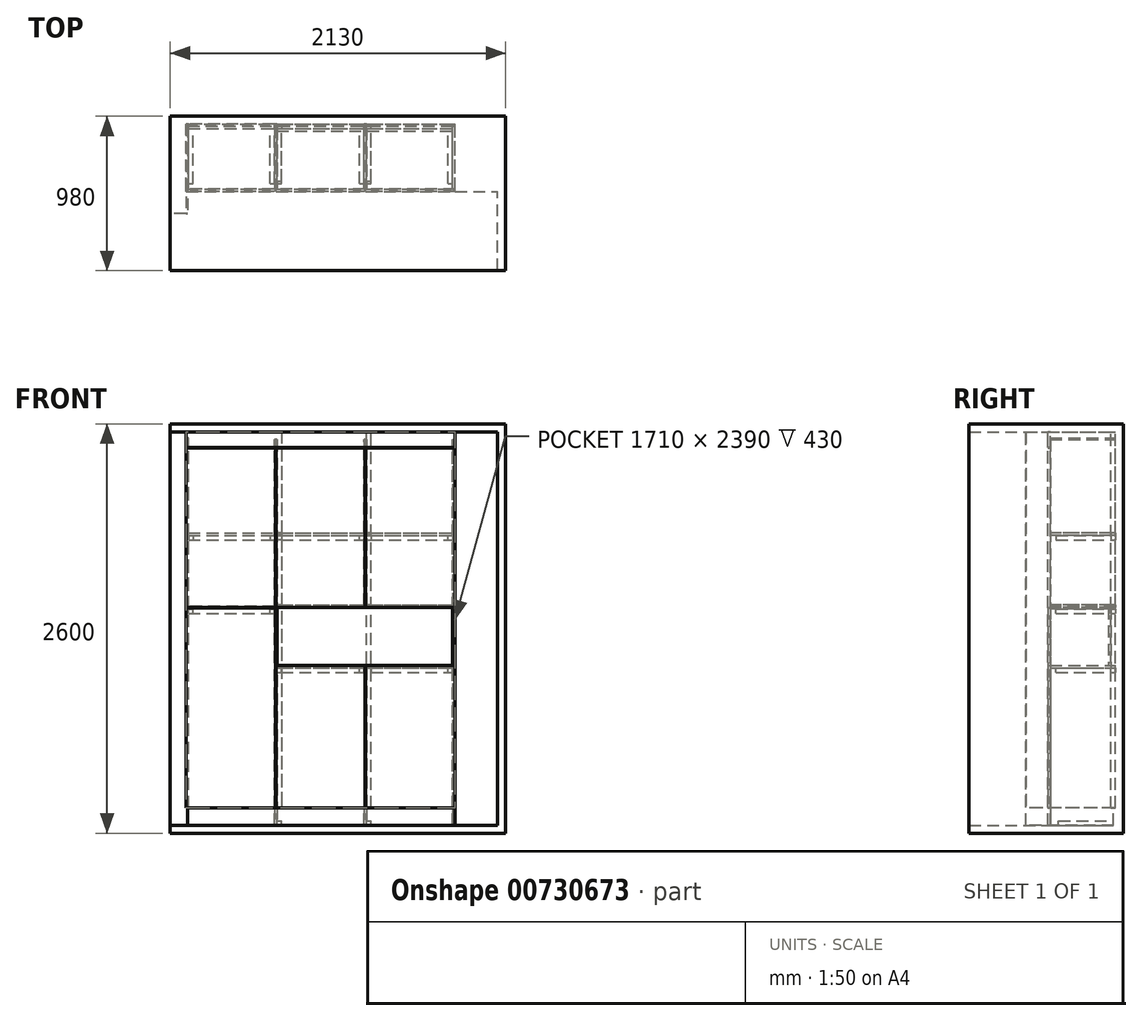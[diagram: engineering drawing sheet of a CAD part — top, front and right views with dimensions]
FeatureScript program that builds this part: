
annotation { "Feature Type Name" : "Feature", "Feature Type Description" : "" }
export const myFeature = defineFeature(function(context is Context, id is Id, definition is map)
    precondition{}
    {
        {
            var Q0;
            Q0=qCreatedBy(makeId("Front.planeOp"),FACE);
            var sketch = newSketch(context, id + "F0", { "sketchPlane" : qUnion([Q0])});
            skLineSegment(sketch, "E0.bottom", {"start": v(0, 0) * mm, "end": v(1710, 0) * mm});
            skLineSegment(sketch, "E0.top", {"start": v(0, 2500) * mm, "end": v(1710, 2500) * mm});
            skLineSegment(sketch, "E0.left", {"start": v(0, 0) * mm, "end": v(0, 2500) * mm});
            skLineSegment(sketch, "E0.right", {"start": v(1710, 0) * mm, "end": v(1710, 2500) * mm});
            skLineSegment(sketch, "E1", {"start": v(1980, -50) * mm, "end": v(-100, -50) * mm});
            skLineSegment(sketch, "E2", {"start": v(-100, -50) * mm, "end": v(-100, 2550) * mm});
            skLineSegment(sketch, "E3", {"start": v(-100, 2550) * mm, "end": v(1980, 2550) * mm});
            skLineSegment(sketch, "E4", {"start": v(1980, 2550) * mm, "end": v(1980, -50) * mm});
            skSolve(sketch);
        }
        {
            var Q0;
            Q0 = qSketchRegion(id + "F0", true);
            extrude(context, id + "F1", {"entities" : qUnion([Q0]), "depth" : 430 * mm, "offsetDistance" : 25 * mm});
        }
        {
            var Q0;
            Q0=makeQuery(id+"F1.opExtrude","CAP_FACE",FACE,{"disambiguationData":[OSD([sQuery(id+"F0.wireOp",EDGE,"E0.bottom"),sQuery(id+"F0.wireOp",EDGE,"E0.top"),sQuery(id+"F0.wireOp",EDGE,"E0.left"),sQuery(id+"F0.wireOp",EDGE,"E0.right"),sQuery(id+"F0.wireOp",EDGE,"E1"),sQuery(id+"F0.wireOp",EDGE,"E2"),sQuery(id+"F0.wireOp",EDGE,"E3"),sQuery(id+"F0.wireOp",EDGE,"E4")])],"isStart":false});
            var sketch = newSketch(context, id + "F2", { "sketchPlane" : qUnion([Q0])});
            skLineSegment(sketch, "E5.bottom", {"start": v(-100, 2550) * mm, "end": v(0, 2550) * mm});
            skLineSegment(sketch, "E5.top", {"start": v(-100, -50) * mm, "end": v(0, -50) * mm});
            skLineSegment(sketch, "E5.left", {"start": v(-100, 2550) * mm, "end": v(-100, -50) * mm});
            skLineSegment(sketch, "E5.right", {"start": v(0, 2550) * mm, "end": v(0, -50) * mm});
            skSolve(sketch);
        }
        {
            var Q0;
            Q0 = qSketchRegion(id + "F2", true);
            extrude(context, id + "F3", {"entities" : qUnion([Q0]), "operationType" : NewBodyOperationType.ADD, "depth" : (570 - 430) * mm, "offsetDistance" : 25 * mm});
        }
        {
            var Q0;
            Q0=makeQuery(id+"F1.opExtrude","CAP_FACE",FACE,{"disambiguationData":[OSD([sQuery(id+"F0.wireOp",EDGE,"E0.bottom"),sQuery(id+"F0.wireOp",EDGE,"E0.top"),sQuery(id+"F0.wireOp",EDGE,"E0.left"),sQuery(id+"F0.wireOp",EDGE,"E0.right"),sQuery(id+"F0.wireOp",EDGE,"E1"),sQuery(id+"F0.wireOp",EDGE,"E2"),sQuery(id+"F0.wireOp",EDGE,"E3"),sQuery(id+"F0.wireOp",EDGE,"E4")])],"isStart":false});
            var sketch = newSketch(context, id + "F4", { "sketchPlane" : qUnion([Q0])});
            skLineSegment(sketch, "E6", {"start": v(1980, 2550) * mm, "end": v(1980, 2500) * mm});
            skLineSegment(sketch, "E7", {"start": v(1980, -50) * mm, "end": v(-100, -50) * mm});
            skLineSegment(sketch, "E8", {"start": v(-100, 2550) * mm, "end": v(1980, 2550) * mm});
            skLineSegment(sketch, "E9", {"start": v(-100, 2550) * mm, "end": v(-100, 2500) * mm});
            skLineSegment(sketch, "E10", {"start": v(-100, 2500) * mm, "end": v(1980, 2500) * mm});
            skLineSegment(sketch, "E11", {"start": v(-100, -50) * mm, "end": v(-100, 0) * mm});
            skLineSegment(sketch, "E12", {"start": v(-100, 0) * mm, "end": v(1980, 0) * mm});
            skLineSegment(sketch, "E13.trimOffspring", {"start": v(1980, 0) * mm, "end": v(1980, -50) * mm});
            skSolve(sketch);
        }
        {
            var Q0;
            Q0 = qSketchRegion(id + "F4", true);
            extrude(context, id + "F5", {"entities" : qUnion([Q0]), "operationType" : NewBodyOperationType.ADD, "depth" : 500 * mm, "offsetDistance" : 25 * mm});
        }
        {
            var Q0;
            Q0=makeQuery(id+"F5.boolean.opBoolean","MERGE",FACE,{"derivedFrom":[makeQuery(id+"F1.opExtrude","SWEPT_FACE",FACE,{"disambiguationData":[OSD([sQuery(id+"F0.wireOp",EDGE,"E4")])]}),makeQuery(id+"F5.opExtrude","SWEPT_FACE",FACE,{"disambiguationData":[OSD([sQuery(id+"F4.wireOp",EDGE,"E6")])]}),makeQuery(id+"F5.opExtrude","SWEPT_FACE",FACE,{"disambiguationData":[OSD([sQuery(id+"F4.wireOp",EDGE,"E13.trimOffspring")])]})]});
            var sketch = newSketch(context, id + "F6", { "sketchPlane" : qUnion([Q0])});
            skLineSegment(sketch, "E14.bottom", {"start": v(-930, 2550) * mm, "end": v(0, 2550) * mm});
            skLineSegment(sketch, "E14.top", {"start": v(-930, -50) * mm, "end": v(0, -50) * mm});
            skLineSegment(sketch, "E14.left", {"start": v(-930, 2550) * mm, "end": v(-930, -50) * mm});
            skLineSegment(sketch, "E14.right", {"start": v(0, 2550) * mm, "end": v(0, -50) * mm});
            skSolve(sketch);
        }
        {
            var Q0;
            Q0 = qSketchRegion(id + "F6", true);
            extrude(context, id + "F7", {"entities" : qUnion([Q0]), "operationType" : NewBodyOperationType.ADD, "depth" : 50 * mm, "offsetDistance" : 25 * mm});
        }
        {
            var Q0;
            Q0=makeQuery(id+"F7.boolean.opBoolean","MERGE",FACE,{"derivedFrom":[makeQuery(id+"F1.opExtrude","CAP_FACE",FACE,{"disambiguationData":[OSD([sQuery(id+"F0.wireOp",EDGE,"E0.bottom"),sQuery(id+"F0.wireOp",EDGE,"E0.top"),sQuery(id+"F0.wireOp",EDGE,"E0.left"),sQuery(id+"F0.wireOp",EDGE,"E0.right"),sQuery(id+"F0.wireOp",EDGE,"E1"),sQuery(id+"F0.wireOp",EDGE,"E2"),sQuery(id+"F0.wireOp",EDGE,"E3"),sQuery(id+"F0.wireOp",EDGE,"E4")])],"isStart":true}),makeQuery(id+"F7.opExtrude","SWEPT_FACE",FACE,{"disambiguationData":[OSD([sQuery(id+"F6.wireOp",EDGE,"E14.right")])]})]});
            var sketch = newSketch(context, id + "F8", { "sketchPlane" : qUnion([Q0])});
            skLineSegment(sketch, "E15.bottom", {"start": v(-2030, 2550) * mm, "end": v(100, 2550) * mm});
            skLineSegment(sketch, "E15.top", {"start": v(-2030, -50) * mm, "end": v(100, -50) * mm});
            skLineSegment(sketch, "E15.left", {"start": v(-2030, 2550) * mm, "end": v(-2030, -50) * mm});
            skLineSegment(sketch, "E15.right", {"start": v(100, 2550) * mm, "end": v(100, -50) * mm});
            skSolve(sketch);
        }
        {
            var Q0;
            Q0 = qSketchRegion(id + "F8", true);
            extrude(context, id + "F9", {"entities" : qUnion([Q0]), "operationType" : NewBodyOperationType.ADD, "depth" : 50 * mm, "offsetDistance" : 25 * mm});
        }
        {
            var Q0;
            Q0=makeQuery(id+"F5.boolean.opBoolean","MERGE",FACE,{"derivedFrom":[makeQuery(id+"F1.opExtrude","SWEPT_FACE",FACE,{"disambiguationData":[OSD([sQuery(id+"F0.wireOp",EDGE,"E0.bottom")])]}),makeQuery(id+"F5.opExtrude","SWEPT_FACE",FACE,{"disambiguationData":[OSD([sQuery(id+"F4.wireOp",EDGE,"E12")])]})]});
            var sketch = newSketch(context, id + "F10", { "sketchPlane" : qUnion([Q0])});
            skLineSegment(sketch, "E16", {"start": v(0, 0) * mm, "end": v(570, 0) * mm});
            skLineSegment(sketch, "E17", {"start": v(570, 0) * mm, "end": v(1140, 0) * mm});
            skLineSegment(sketch, "E18", {"start": v(1140, 0) * mm, "end": v(1710, 0) * mm});
            skSolve(sketch);
        }
        {
            var Q0;
            Q0=makeQuery(id+"F3.opExtrude","CAP_FACE",FACE,{"disambiguationData":[OSD([sQuery(id+"F2.wireOp",EDGE,"E5.bottom"),sQuery(id+"F2.wireOp",EDGE,"E5.top"),sQuery(id+"F2.wireOp",EDGE,"E5.left"),sQuery(id+"F2.wireOp",EDGE,"E5.right")])],"isStart":false});
            var sketch = newSketch(context, id + "F11", { "sketchPlane" : qUnion([Q0])});
            skLineSegment(sketch, "E19.bottom", {"start": v(0, 0) * mm, "end": v(10, 0) * mm});
            skLineSegment(sketch, "E19.top", {"start": v(0, 110) * mm, "end": v(10, 110) * mm});
            skLineSegment(sketch, "E19.left", {"start": v(0, 0) * mm, "end": v(0, 110) * mm});
            skLineSegment(sketch, "E19.right", {"start": v(10, 0) * mm, "end": v(10, 110) * mm});
            skSolve(sketch);
        }
        {
            var Q0;
            Q0 = qSketchRegion(id + "F11", true);
            var Q1;
            Q1=makeQuery(id+"F9.opExtrude","CAP_FACE",FACE,{"disambiguationData":[OSD([sQuery(id+"F8.wireOp",EDGE,"E15.bottom"),sQuery(id+"F8.wireOp",EDGE,"E15.top"),sQuery(id+"F8.wireOp",EDGE,"E15.left"),sQuery(id+"F8.wireOp",EDGE,"E15.right")])],"isStart":true});
            extrude(context, id + "F12", {"entities" : qUnion([Q0]), "endBound" : BoundingType.UP_TO_SURFACE, "oppositeDirection" : true, "depth" : 25 * mm, "endBoundEntityFace" : qUnion([Q1]), "offsetDistance" : 25 * mm});
        }
        {
            var Q0;
            Q0=makeQuery(id+"F9.opExtrude","CAP_FACE",FACE,{"disambiguationData":[OSD([sQuery(id+"F8.wireOp",EDGE,"E15.bottom"),sQuery(id+"F8.wireOp",EDGE,"E15.top"),sQuery(id+"F8.wireOp",EDGE,"E15.left"),sQuery(id+"F8.wireOp",EDGE,"E15.right")])],"isStart":true});
            var sketch = newSketch(context, id + "F13", { "sketchPlane" : qUnion([Q0])});
            skLineSegment(sketch, "E20.bottom", {"start": v(10, 110) * mm, "end": v(1710, 110) * mm});
            skLineSegment(sketch, "E20.top", {"start": v(10, 0) * mm, "end": v(1710, 0) * mm});
            skLineSegment(sketch, "E20.left", {"start": v(10, 110) * mm, "end": v(10, 0) * mm});
            skLineSegment(sketch, "E20.right", {"start": v(1710, 110) * mm, "end": v(1710, 0) * mm});
            skSolve(sketch);
        }
        {
            var Q0;
            Q0 = qSketchRegion(id + "F13", true);
            extrude(context, id + "F14", {"entities" : qUnion([Q0]), "operationType" : NewBodyOperationType.ADD, "depth" : 12 * mm, "offsetDistance" : 25 * mm});
        }
        {
            var Q0;
            Q0=makeQuery(id+"F1.opExtrude","CAP_FACE",FACE,{"disambiguationData":[OSD([sQuery(id+"F0.wireOp",EDGE,"E0.bottom"),sQuery(id+"F0.wireOp",EDGE,"E0.top"),sQuery(id+"F0.wireOp",EDGE,"E0.left"),sQuery(id+"F0.wireOp",EDGE,"E0.right"),sQuery(id+"F0.wireOp",EDGE,"E1"),sQuery(id+"F0.wireOp",EDGE,"E2"),sQuery(id+"F0.wireOp",EDGE,"E3"),sQuery(id+"F0.wireOp",EDGE,"E4")])],"isStart":false});
            var sketch = newSketch(context, id + "F15", { "sketchPlane" : qUnion([Q0])});
            skLineSegment(sketch, "E21.bottom", {"start": v(1710, 2500) * mm, "end": v(0, 2500) * mm});
            skLineSegment(sketch, "E21.top", {"start": v(1710, 2400) * mm, "end": v(0, 2400) * mm});
            skLineSegment(sketch, "E21.left", {"start": v(1710, 2500) * mm, "end": v(1710, 2400) * mm});
            skLineSegment(sketch, "E21.right", {"start": v(0, 2500) * mm, "end": v(0, 2400) * mm});
            skSolve(sketch);
        }
        {
            var Q0;
            Q0 = qSketchRegion(id + "F15", true);
            extrude(context, id + "F16", {"entities" : qUnion([Q0]), "oppositeDirection" : true, "depth" : 16 * mm, "offsetDistance" : 25 * mm});
        }
        {
            var Q0;
            Q0=makeQuery(id+"F3.boolean.opBoolean","MERGE",FACE,{"derivedFrom":[makeQuery(id+"F1.opExtrude","SWEPT_FACE",FACE,{"disambiguationData":[OSD([sQuery(id+"F0.wireOp",EDGE,"E0.left")])]}),makeQuery(id+"F3.opExtrude","SWEPT_FACE",FACE,{"disambiguationData":[OSD([sQuery(id+"F2.wireOp",EDGE,"E5.right")])]})]});
            var sketch = newSketch(context, id + "F17", { "sketchPlane" : qUnion([Q0])});
            skLineSegment(sketch, "E22.bottom", {"start": v(-414, 110) * mm, "end": v(0, 110) * mm});
            skLineSegment(sketch, "E22.top", {"start": v(-414, 2460) * mm, "end": v(0, 2460) * mm});
            skLineSegment(sketch, "E22.left", {"start": v(-414, 110) * mm, "end": v(-414, 2460) * mm});
            skLineSegment(sketch, "E22.right", {"start": v(0, 110) * mm, "end": v(0, 2460) * mm});
            skSolve(sketch);
        }
        {
            var Q0;
            Q0 = qSketchRegion(id + "F17", true);
            extrude(context, id + "F18", {"entities" : qUnion([Q0]), "depth" : 16 * mm, "offsetDistance" : 25 * mm});
        }
        {
            var Q0;
            Q0=sQuery(id+"F10.wireOp",VERTEX,"E17.start");
            var Q1;
            Q1=sQuery(id+"F10.wireOp",EDGE,"E16");
            cPlane(context, id + "F19", {"entities" : qUnion([Q0, Q1]), "cplaneType" : CPlaneType.LINE_POINT, "offset" : 25 * mm, "width" : 150 * mm, "height" : 150 * mm});
        }
        {
            var Q0;
            Q0=sQuery(id+"F10.wireOp",VERTEX,"E18.start");
            var Q1;
            Q1=sQuery(id+"F10.wireOp",EDGE,"E17");
            cPlane(context, id + "F20", {"entities" : qUnion([Q0, Q1]), "cplaneType" : CPlaneType.LINE_POINT, "offset" : 25 * mm, "width" : 150 * mm, "height" : 150 * mm});
        }
        {
            var Q0;
            Q0=qCreatedBy(id+"F19.planeOp",FACE);
            var sketch = newSketch(context, id + "F21", { "sketchPlane" : qUnion([Q0])});
            skLineSegment(sketch, "E23", {"start": v(-414, 0) * mm, "end": v(-414, 2450) * mm});
            skLineSegment(sketch, "E24", {"start": v(-414, 2450) * mm, "end": v(0, 2450) * mm});
            skLineSegment(sketch, "E25", {"start": v(0, 2450) * mm, "end": v(0, 112) * mm});
            skLineSegment(sketch, "E26", {"start": v(0, 112) * mm, "end": v(-14, 112) * mm});
            skLineSegment(sketch, "E27", {"start": v(-14, 112) * mm, "end": v(-14, 0) * mm});
            skLineSegment(sketch, "E28", {"start": v(-14, 0) * mm, "end": v(-414, 0) * mm});
            skPoint(sketch, "E29", {"position": v(0, 110) * mm});
            skPoint(sketch, "E30", {"position": v(-12, 0) * mm});
            skPoint(sketch, "E31", {"position": v(0, 2500) * mm});
            skSolve(sketch);
        }
        {
            var Q0;
            Q0 = qSketchRegion(id + "F21", true);
            extrude(context, id + "F22", {"entities" : qUnion([Q0]), "endBound" : BoundingType.SYMMETRIC, "depth" : 16 * mm, "offsetDistance" : 25 * mm});
        }
        {
            var Q0;
            Q0=qCreatedBy(id+"F20.planeOp",FACE);
            var sketch = newSketch(context, id + "F23", { "sketchPlane" : qUnion([Q0])});
            skLineSegment(sketch, "E32.0.0", {"start": v(-414, 0) * mm, "end": v(-14, 0) * mm});
            skLineSegment(sketch, "E32.0.1", {"start": v(-14, 0) * mm, "end": v(-14, 112) * mm});
            skLineSegment(sketch, "E32.0.2", {"start": v(-14, 112) * mm, "end": v(0, 112) * mm});
            skLineSegment(sketch, "E32.0.3", {"start": v(0, 112) * mm, "end": v(0, 1000) * mm});
            skLineSegment(sketch, "E32.0.4", {"start": v(0, 2450) * mm, "end": v(-414, 2450) * mm});
            skLineSegment(sketch, "E32.0.5", {"start": v(-414, 2450) * mm, "end": v(-414, 1400) * mm});
            skLineSegment(sketch, "E33", {"start": v(-414, 1000) * mm, "end": v(0, 1000) * mm});
            skLineSegment(sketch, "E34", {"start": v(-414, 1400) * mm, "end": v(0, 1400) * mm});
            skLineSegment(sketch, "E35.trimOffspring", {"start": v(-414, 1000) * mm, "end": v(-414, 0) * mm});
            skLineSegment(sketch, "E36.trimOffspring", {"start": v(0, 1400) * mm, "end": v(0, 2450) * mm});
            skSolve(sketch);
        }
        {
            var Q0;
            Q0 = qSketchRegion(id + "F23", true);
            extrude(context, id + "F24", {"entities" : qUnion([Q0]), "endBound" : BoundingType.SYMMETRIC, "depth" : 16 * mm, "offsetDistance" : 25 * mm});
        }
        {
            var Q0;
            Q0=makeQuery(id+"F1.opExtrude","SWEPT_FACE",FACE,{"disambiguationData":[OSD([sQuery(id+"F0.wireOp",EDGE,"E0.right")])]});
            var sketch = newSketch(context, id + "F25", { "sketchPlane" : qUnion([Q0])});
            skLineSegment(sketch, "E37.0", {"start": v(414, 2450) * mm, "end": v(0, 2450) * mm});
            skLineSegment(sketch, "E38", {"start": v(414, 2450) * mm, "end": v(414, 0) * mm});
            skLineSegment(sketch, "E39", {"start": v(414, 0) * mm, "end": v(14, 0) * mm});
            skLineSegment(sketch, "E40", {"start": v(14, 0) * mm, "end": v(14, 112) * mm});
            skLineSegment(sketch, "E41", {"start": v(14, 112) * mm, "end": v(0, 112) * mm});
            skLineSegment(sketch, "E42", {"start": v(0, 112) * mm, "end": v(0, 2450) * mm});
            skSolve(sketch);
        }
        {
            var Q0;
            Q0 = qSketchRegion(id + "F25", true);
            extrude(context, id + "F26", {"entities" : qUnion([Q0]), "depth" : 16 * mm, "offsetDistance" : 25 * mm});
        }
        {
            var Q0;
            Q0=makeQuery(id+"F24.opExtrude","SWEPT_FACE",FACE,{"disambiguationData":[OSD([sQuery(id+"F23.wireOp",EDGE,"E34")])]});
            var sketch = newSketch(context, id + "F27", { "sketchPlane" : qUnion([Q0])});
            skLineSegment(sketch, "E43.bottom", {"start": v(578, 0) * mm, "end": v(1694, 0) * mm});
            skLineSegment(sketch, "E43.top", {"start": v(578, 414) * mm, "end": v(1694, 414) * mm});
            skLineSegment(sketch, "E43.left", {"start": v(578, 0) * mm, "end": v(578, 414) * mm});
            skLineSegment(sketch, "E43.right", {"start": v(1694, 0) * mm, "end": v(1694, 414) * mm});
            skSolve(sketch);
        }
        {
            var Q0;
            Q0 = qSketchRegion(id + "F27", true);
            extrude(context, id + "F28", {"entities" : qUnion([Q0]), "depth" : 16 * mm, "offsetDistance" : 25 * mm});
        }
        {
            var Q0;
            Q0=makeQuery(id+"F24.opExtrude","SWEPT_FACE",FACE,{"disambiguationData":[OSD([sQuery(id+"F23.wireOp",EDGE,"E33")])]});
            var sketch = newSketch(context, id + "F29", { "sketchPlane" : qUnion([Q0])});
            skLineSegment(sketch, "E44.bottom", {"start": v(578, -414) * mm, "end": v(1694, -414) * mm});
            skLineSegment(sketch, "E44.top", {"start": v(578, 0) * mm, "end": v(1694, 0) * mm});
            skLineSegment(sketch, "E44.left", {"start": v(578, -414) * mm, "end": v(578, 0) * mm});
            skLineSegment(sketch, "E44.right", {"start": v(1694, -414) * mm, "end": v(1694, 0) * mm});
            skSolve(sketch);
        }
        {
            var Q0;
            Q0 = qSketchRegion(id + "F29", true);
            extrude(context, id + "F30", {"entities" : qUnion([Q0]), "depth" : 16 * mm, "offsetDistance" : 25 * mm});
        }
        {
            var Q0;
            Q0=makeQuery(id+"F22.opExtrude","SWEPT_FACE",FACE,{"disambiguationData":[OSD([sQuery(id+"F21.wireOp",EDGE,"E23")])]});
            var sketch = newSketch(context, id + "F31", { "sketchPlane" : qUnion([Q0])});
            skLineSegment(sketch, "E45.bottom", {"start": v(1710, 0) * mm, "end": v(10, 0) * mm});
            skLineSegment(sketch, "E45.top", {"start": v(1710, 110) * mm, "end": v(10, 110) * mm});
            skLineSegment(sketch, "E45.left", {"start": v(1710, 0) * mm, "end": v(1710, 110) * mm});
            skLineSegment(sketch, "E45.right", {"start": v(10, 0) * mm, "end": v(10, 110) * mm});
            skSolve(sketch);
        }
        {
            var Q0;
            Q0 = qSketchRegion(id + "F31", true);
            extrude(context, id + "F32", {"entities" : qUnion([Q0]), "depth" : 16 * mm, "offsetDistance" : 25 * mm});
        }
        {
            var Q0;
            Q0=makeQuery(id+"F28.opExtrude","CAP_FACE",FACE,{"disambiguationData":[OSD([sQuery(id+"F27.wireOp",EDGE,"E43.bottom"),sQuery(id+"F27.wireOp",EDGE,"E43.top"),sQuery(id+"F27.wireOp",EDGE,"E43.left"),sQuery(id+"F27.wireOp",EDGE,"E43.right")])],"isStart":true});
            cPlane(context, id + "F33", {"entities" : qUnion([Q0]), "cplaneType" : CPlaneType.OFFSET, "offset" : 9 * mm, "oppositeDirection" : true, "width" : 150 * mm, "height" : 150 * mm});
        }
        {
            var Q0;
            Q0=qCreatedBy(id+"F33.planeOp",FACE);
            var sketch = newSketch(context, id + "F34", { "sketchPlane" : qUnion([Q0])});
            skLineSegment(sketch, "E46.bottom", {"start": v(562, 0) * mm, "end": v(16, 0) * mm});
            skLineSegment(sketch, "E46.top", {"start": v(562, -414) * mm, "end": v(16, -414) * mm});
            skLineSegment(sketch, "E46.left", {"start": v(562, 0) * mm, "end": v(562, -414) * mm});
            skLineSegment(sketch, "E46.right", {"start": v(16, 0) * mm, "end": v(16, -414) * mm});
            skSolve(sketch);
        }
        {
            var Q0;
            Q0 = qSketchRegion(id + "F34", true);
            extrude(context, id + "F35", {"entities" : qUnion([Q0]), "oppositeDirection" : true, "depth" : 16 * mm, "offsetDistance" : 25 * mm});
        }
        {
            var Q0;
            Q0=makeQuery(id+"F22.opExtrude","SWEPT_FACE",FACE,{"disambiguationData":[OSD([sQuery(id+"F21.wireOp",EDGE,"E23")])]});
            var sketch = newSketch(context, id + "F36", { "sketchPlane" : qUnion([Q0])});
            skLineSegment(sketch, "E47.bottom", {"start": v(2, 2398) * mm, "end": v(568, 2398) * mm});
            skLineSegment(sketch, "E47.top", {"start": v(2, 1384) * mm, "end": v(568, 1384) * mm});
            skLineSegment(sketch, "E47.left", {"start": v(2, 2398) * mm, "end": v(2, 1384) * mm});
            skLineSegment(sketch, "E47.right", {"start": v(568, 2398) * mm, "end": v(568, 1384) * mm});
            skLineSegment(sketch, "E48", {"start": v(562, 1400) * mm, "end": v(578, 1400) * mm, "construction": true});
            skPoint(sketch, "E49", {"position": v(570, 1400) * mm});
            skLineSegment(sketch, "E50.bottom", {"start": v(572, 1384) * mm, "end": v(1138, 1384) * mm});
            skLineSegment(sketch, "E50.top", {"start": v(572, 2398) * mm, "end": v(1138, 2398) * mm});
            skLineSegment(sketch, "E50.left", {"start": v(572, 1384) * mm, "end": v(572, 2398) * mm});
            skLineSegment(sketch, "E50.right", {"start": v(1138, 1384) * mm, "end": v(1138, 2398) * mm});
            skLineSegment(sketch, "E51", {"start": v(1132, 1400) * mm, "end": v(1148, 1400) * mm, "construction": true});
            skPoint(sketch, "E52", {"position": v(1140, 1400) * mm});
            skLineSegment(sketch, "E53.bottom", {"start": v(1142, 1384) * mm, "end": v(1708, 1384) * mm});
            skLineSegment(sketch, "E53.top", {"start": v(1142, 2398) * mm, "end": v(1708, 2398) * mm});
            skLineSegment(sketch, "E53.left", {"start": v(1142, 1384) * mm, "end": v(1142, 2398) * mm});
            skLineSegment(sketch, "E53.right", {"start": v(1708, 1384) * mm, "end": v(1708, 2398) * mm});
            skSolve(sketch);
        }
        {
            var Q0;
            Q0 = qSketchRegion(id + "F36", true);
            extrude(context, id + "F37", {"entities" : qUnion([Q0]), "depth" : 16 * mm, "offsetDistance" : 25 * mm});
        }
        {
            var Q0;
            Q0=makeQuery(id+"F22.opExtrude","SWEPT_FACE",FACE,{"disambiguationData":[OSD([sQuery(id+"F21.wireOp",EDGE,"E23")])]});
            var sketch = newSketch(context, id + "F38", { "sketchPlane" : qUnion([Q0])});
            skLineSegment(sketch, "E54.top", {"start": v(2, 112) * mm, "end": v(568, 112) * mm});
            skLineSegment(sketch, "E54.left", {"start": v(2, 1382) * mm, "end": v(2, 112) * mm});
            skLineSegment(sketch, "E54.right", {"start": v(568, 1382) * mm, "end": v(568, 112) * mm});
            skLineSegment(sketch, "E55.bottom", {"start": v(572, 112) * mm, "end": v(1138, 112) * mm});
            skLineSegment(sketch, "E55.top", {"start": v(572, 1016) * mm, "end": v(1138, 1016) * mm});
            skLineSegment(sketch, "E55.left", {"start": v(572, 112) * mm, "end": v(572, 1016) * mm});
            skLineSegment(sketch, "E55.right", {"start": v(1138, 112) * mm, "end": v(1138, 1016) * mm});
            skLineSegment(sketch, "E56.bottom", {"start": v(1142, 1016) * mm, "end": v(1708, 1016) * mm});
            skLineSegment(sketch, "E56.top", {"start": v(1142, 112) * mm, "end": v(1708, 112) * mm});
            skLineSegment(sketch, "E56.left", {"start": v(1142, 1016) * mm, "end": v(1142, 112) * mm});
            skLineSegment(sketch, "E56.right", {"start": v(1708, 1016) * mm, "end": v(1708, 112) * mm});
            skLineSegment(sketch, "E57", {"start": v(1132, 1000) * mm, "end": v(1148, 1000) * mm, "construction": true});
            skLineSegment(sketch, "E58", {"start": v(1140, 810.49) * mm, "end": v(1140, 1000) * mm, "construction": true});
            skLineSegment(sketch, "E59", {"start": v(2, 1382) * mm, "end": v(568, 1382) * mm});
            skSolve(sketch);
        }
        {
            var Q0;
            Q0 = qSketchRegion(id + "F38", true);
            extrude(context, id + "F39", {"entities" : qUnion([Q0]), "depth" : 16 * mm, "offsetDistance" : 25 * mm});
        }
        {
            var Q0;
            Q0=makeQuery(id+"F18.opExtrude","SWEPT_FACE",FACE,{"disambiguationData":[OSD([sQuery(id+"F17.wireOp",EDGE,"E22.left")])]});
            var sketch = newSketch(context, id + "F40", { "sketchPlane" : qUnion([Q0])});
            skLineSegment(sketch, "E60.bottom", {"start": v(16, 1857) * mm, "end": v(562, 1857) * mm});
            skLineSegment(sketch, "E60.top", {"start": v(16, 1841) * mm, "end": v(562, 1841) * mm});
            skLineSegment(sketch, "E60.left", {"start": v(16, 1857) * mm, "end": v(16, 1841) * mm});
            skLineSegment(sketch, "E60.right", {"start": v(562, 1857) * mm, "end": v(562, 1841) * mm});
            skLineSegment(sketch, "E61.bottom", {"start": v(578, 1857) * mm, "end": v(1132, 1857) * mm});
            skLineSegment(sketch, "E61.top", {"start": v(578, 1841) * mm, "end": v(1132, 1841) * mm});
            skLineSegment(sketch, "E61.left", {"start": v(578, 1857) * mm, "end": v(578, 1841) * mm});
            skLineSegment(sketch, "E61.right", {"start": v(1132, 1857) * mm, "end": v(1132, 1841) * mm});
            skLineSegment(sketch, "E62.bottom", {"start": v(1148, 1857) * mm, "end": v(1694, 1857) * mm});
            skLineSegment(sketch, "E62.top", {"start": v(1148, 1841) * mm, "end": v(1694, 1841) * mm});
            skLineSegment(sketch, "E62.left", {"start": v(1148, 1857) * mm, "end": v(1148, 1841) * mm});
            skLineSegment(sketch, "E62.right", {"start": v(1694, 1857) * mm, "end": v(1694, 1841) * mm});
            skSolve(sketch);
        }
        {
            var Q0;
            Q0=makeQuery(id+"F40.imprint","IMPRINT",FACE,{"disambiguationData":[TD([[makeQuery(id+"F40.imprint","IMPRINT",EDGE,{"derivedFrom":sQuery(id+"F40.wireOp",EDGE,"E60.bottom")}),-1.0]])]});
            var Q1;
            Q1=makeQuery(id+"F40.imprint","IMPRINT",FACE,{"disambiguationData":[TD([[makeQuery(id+"F40.imprint","IMPRINT",EDGE,{"derivedFrom":sQuery(id+"F40.wireOp",EDGE,"E61.bottom")}),-1.0]])]});
            var Q2;
            Q2=makeQuery(id+"F40.imprint","IMPRINT",FACE,{"disambiguationData":[TD([[makeQuery(id+"F40.imprint","IMPRINT",EDGE,{"derivedFrom":sQuery(id+"F40.wireOp",EDGE,"E62.bottom")}),-1.0]])]});
            extrude(context, id + "F41", {"entities" : qUnion([Q0, Q1, Q2]), "endBound" : BoundingType.UP_TO_NEXT, "oppositeDirection" : true, "depth" : 25 * mm, "offsetDistance" : 25 * mm});
        }
        {
            var Q0;
            Q0=makeQuery(id+"F9.opExtrude","CAP_FACE",FACE,{"disambiguationData":[OSD([sQuery(id+"F8.wireOp",EDGE,"E15.bottom"),sQuery(id+"F8.wireOp",EDGE,"E15.top"),sQuery(id+"F8.wireOp",EDGE,"E15.left"),sQuery(id+"F8.wireOp",EDGE,"E15.right")])],"isStart":true});
            var sketch = newSketch(context, id + "F42", { "sketchPlane" : qUnion([Q0])});
            skLineSegment(sketch, "E63.bottom", {"start": v(578, 2500) * mm, "end": v(606, 2500) * mm});
            skLineSegment(sketch, "E63.top", {"start": v(578, 110) * mm, "end": v(606, 110) * mm});
            skLineSegment(sketch, "E63.left", {"start": v(578, 2500) * mm, "end": v(578, 110) * mm});
            skLineSegment(sketch, "E63.right", {"start": v(606, 2500) * mm, "end": v(606, 110) * mm});
            skLineSegment(sketch, "E64.bottom", {"start": v(1148, 110) * mm, "end": v(1176, 110) * mm});
            skLineSegment(sketch, "E64.top", {"start": v(1148, 2500) * mm, "end": v(1176, 2500) * mm});
            skLineSegment(sketch, "E64.left", {"start": v(1148, 110) * mm, "end": v(1148, 2500) * mm});
            skLineSegment(sketch, "E64.right", {"start": v(1176, 110) * mm, "end": v(1176, 2500) * mm});
            skSolve(sketch);
        }
        {
            var Q0;
            Q0 = qSketchRegion(id + "F42", true);
            extrude(context, id + "F43", {"entities" : qUnion([Q0]), "depth" : 28 * mm, "offsetDistance" : 25 * mm});
        }
        {
            var Q0;
            Q0=makeQuery(id+"F43.opExtrude","CAP_FACE",FACE,{"disambiguationData":[OSD([sQuery(id+"F42.wireOp",EDGE,"E64.bottom"),sQuery(id+"F42.wireOp",EDGE,"E64.top"),sQuery(id+"F42.wireOp",EDGE,"E64.left"),sQuery(id+"F42.wireOp",EDGE,"E64.right")])],"isStart":false});
            var sketch = newSketch(context, id + "F44", { "sketchPlane" : qUnion([Q0])});
            skLineSegment(sketch, "E65.bottom", {"start": v(578, 1384) * mm, "end": v(1694, 1384) * mm});
            skLineSegment(sketch, "E65.top", {"start": v(578, 1016) * mm, "end": v(1694, 1016) * mm});
            skLineSegment(sketch, "E65.left", {"start": v(578, 1384) * mm, "end": v(578, 1016) * mm});
            skLineSegment(sketch, "E65.right", {"start": v(1694, 1384) * mm, "end": v(1694, 1016) * mm});
            skSolve(sketch);
        }
        {
            var Q0;
            Q0 = qSketchRegion(id + "F44", true);
            extrude(context, id + "F45", {"entities" : qUnion([Q0]), "depth" : 18 * mm, "offsetDistance" : 25 * mm});
        }
        {
            var Q0;
            Q0=makeQuery(id+"F43.opExtrude","SWEPT_BODY",BODY,{"disambiguationData":[OSD([sQuery(id+"F42.wireOp",EDGE,"E63.bottom"),sQuery(id+"F42.wireOp",EDGE,"E63.top"),sQuery(id+"F42.wireOp",EDGE,"E63.left"),sQuery(id+"F42.wireOp",EDGE,"E63.right")])]});
            var Q1;
            Q1=makeQuery(id+"F43.opExtrude","SWEPT_BODY",BODY,{"disambiguationData":[OSD([sQuery(id+"F42.wireOp",EDGE,"E64.bottom"),sQuery(id+"F42.wireOp",EDGE,"E64.top"),sQuery(id+"F42.wireOp",EDGE,"E64.left"),sQuery(id+"F42.wireOp",EDGE,"E64.right")])]});
            var Q2;
            Q2=makeQuery(id+"F28.opExtrude","SWEPT_BODY",BODY,{"disambiguationData":[OSD([sQuery(id+"F27.wireOp",EDGE,"E43.bottom"),sQuery(id+"F27.wireOp",EDGE,"E43.top"),sQuery(id+"F27.wireOp",EDGE,"E43.left"),sQuery(id+"F27.wireOp",EDGE,"E43.right")])]});
            var Q3;
            Q3=makeQuery(id+"F41.opExtrude","SWEPT_BODY",BODY,{"disambiguationData":[OSD([sQuery(id+"F40.wireOp",EDGE,"E61.bottom"),sQuery(id+"F40.wireOp",EDGE,"E61.top"),sQuery(id+"F40.wireOp",EDGE,"E61.left"),sQuery(id+"F40.wireOp",EDGE,"E61.right")])]});
            var Q4;
            Q4=makeQuery(id+"F41.opExtrude","SWEPT_BODY",BODY,{"disambiguationData":[OSD([sQuery(id+"F40.wireOp",EDGE,"E62.bottom"),sQuery(id+"F40.wireOp",EDGE,"E62.top"),sQuery(id+"F40.wireOp",EDGE,"E62.left"),sQuery(id+"F40.wireOp",EDGE,"E62.right")])]});
            var Q5;
            Q5=makeQuery(id+"F30.opExtrude","SWEPT_BODY",BODY,{"disambiguationData":[OSD([sQuery(id+"F29.wireOp",EDGE,"E44.bottom"),sQuery(id+"F29.wireOp",EDGE,"E44.top"),sQuery(id+"F29.wireOp",EDGE,"E44.left"),sQuery(id+"F29.wireOp",EDGE,"E44.right")])]});
            booleanBodies(context, id + "F46", {"operationType" : BooleanOperationType.SUBTRACTION, "tools" : qUnion([Q0, Q1]), "targets" : qUnion([Q2, Q3, Q4, Q5]), "keepTools" : true});
        }
        {
            var Q0;
            Q0=makeQuery(id+"F9.opExtrude","CAP_FACE",FACE,{"disambiguationData":[OSD([sQuery(id+"F8.wireOp",EDGE,"E15.bottom"),sQuery(id+"F8.wireOp",EDGE,"E15.top"),sQuery(id+"F8.wireOp",EDGE,"E15.left"),sQuery(id+"F8.wireOp",EDGE,"E15.right")])],"isStart":true});
            var sketch = newSketch(context, id + "F47", { "sketchPlane" : qUnion([Q0])});
            skLineSegment(sketch, "E66.bottom", {"start": v(16, 1841) * mm, "end": v(562, 1841) * mm});
            skLineSegment(sketch, "E66.top", {"start": v(16, 1813) * mm, "end": v(562, 1813) * mm});
            skLineSegment(sketch, "E66.left", {"start": v(16, 1841) * mm, "end": v(16, 1813) * mm});
            skLineSegment(sketch, "E66.right", {"start": v(562, 1841) * mm, "end": v(562, 1813) * mm});
            skLineSegment(sketch, "E67.bottom", {"start": v(606, 1841) * mm, "end": v(1132, 1841) * mm});
            skLineSegment(sketch, "E67.top", {"start": v(606, 1813) * mm, "end": v(1132, 1813) * mm});
            skLineSegment(sketch, "E67.left", {"start": v(606, 1841) * mm, "end": v(606, 1813) * mm});
            skLineSegment(sketch, "E67.right", {"start": v(1132, 1841) * mm, "end": v(1132, 1813) * mm});
            skLineSegment(sketch, "E68.bottom", {"start": v(1176, 1841) * mm, "end": v(1694, 1841) * mm});
            skLineSegment(sketch, "E68.top", {"start": v(1176, 1813) * mm, "end": v(1694, 1813) * mm});
            skLineSegment(sketch, "E68.left", {"start": v(1176, 1841) * mm, "end": v(1176, 1813) * mm});
            skLineSegment(sketch, "E68.right", {"start": v(1694, 1841) * mm, "end": v(1694, 1813) * mm});
            skLineSegment(sketch, "E69.bottom", {"start": v(16, 1375) * mm, "end": v(562, 1375) * mm});
            skLineSegment(sketch, "E69.top", {"start": v(16, 1347) * mm, "end": v(562, 1347) * mm});
            skLineSegment(sketch, "E69.left", {"start": v(16, 1375) * mm, "end": v(16, 1347) * mm});
            skLineSegment(sketch, "E69.right", {"start": v(562, 1375) * mm, "end": v(562, 1347) * mm});
            skLineSegment(sketch, "E70.bottom", {"start": v(606, 1000) * mm, "end": v(1132, 1000) * mm});
            skLineSegment(sketch, "E70.top", {"start": v(606, 972) * mm, "end": v(1132, 972) * mm});
            skLineSegment(sketch, "E70.left", {"start": v(606, 1000) * mm, "end": v(606, 972) * mm});
            skLineSegment(sketch, "E70.right", {"start": v(1132, 1000) * mm, "end": v(1132, 972) * mm});
            skLineSegment(sketch, "E71.bottom", {"start": v(1176, 1000) * mm, "end": v(1694, 1000) * mm});
            skLineSegment(sketch, "E71.top", {"start": v(1176, 972) * mm, "end": v(1694, 972) * mm});
            skLineSegment(sketch, "E71.left", {"start": v(1176, 1000) * mm, "end": v(1176, 972) * mm});
            skLineSegment(sketch, "E71.right", {"start": v(1694, 1000) * mm, "end": v(1694, 972) * mm});
            skSolve(sketch);
        }
        {
            var Q0;
            Q0 = qSketchRegion(id + "F47", true);
            extrude(context, id + "F48", {"entities" : qUnion([Q0]), "depth" : 28 * mm, "offsetDistance" : 25 * mm});
        }
        {
            var Q0;
            Q0=makeQuery(id+"F48.opExtrude","CAP_FACE",FACE,{"disambiguationData":[OSD([sQuery(id+"F47.wireOp",EDGE,"E66.bottom"),sQuery(id+"F47.wireOp",EDGE,"E66.top"),sQuery(id+"F47.wireOp",EDGE,"E66.left"),sQuery(id+"F47.wireOp",EDGE,"E66.right")])],"isStart":false});
            var sketch = newSketch(context, id + "F49", { "sketchPlane" : qUnion([Q0])});
            skLineSegment(sketch, "E72.bottom", {"start": v(16, 1841) * mm, "end": v(44, 1841) * mm});
            skLineSegment(sketch, "E72.top", {"start": v(16, 1813) * mm, "end": v(44, 1813) * mm});
            skLineSegment(sketch, "E72.left", {"start": v(16, 1841) * mm, "end": v(16, 1813) * mm});
            skLineSegment(sketch, "E72.right", {"start": v(44, 1841) * mm, "end": v(44, 1813) * mm});
            skLineSegment(sketch, "E73.bottom", {"start": v(562, 1841) * mm, "end": v(534, 1841) * mm});
            skLineSegment(sketch, "E73.top", {"start": v(562, 1813) * mm, "end": v(534, 1813) * mm});
            skLineSegment(sketch, "E73.left", {"start": v(562, 1841) * mm, "end": v(562, 1813) * mm});
            skLineSegment(sketch, "E73.right", {"start": v(534, 1841) * mm, "end": v(534, 1813) * mm});
            skLineSegment(sketch, "E74.bottom", {"start": v(606, 1813) * mm, "end": v(578, 1813) * mm});
            skLineSegment(sketch, "E74.top", {"start": v(606, 1841) * mm, "end": v(578, 1841) * mm});
            skLineSegment(sketch, "E74.left", {"start": v(606, 1813) * mm, "end": v(606, 1841) * mm});
            skLineSegment(sketch, "E74.right", {"start": v(578, 1813) * mm, "end": v(578, 1841) * mm});
            skLineSegment(sketch, "E75.bottom", {"start": v(1104, 1813) * mm, "end": v(1132, 1813) * mm});
            skLineSegment(sketch, "E75.top", {"start": v(1104, 1841) * mm, "end": v(1132, 1841) * mm});
            skLineSegment(sketch, "E75.left", {"start": v(1104, 1813) * mm, "end": v(1104, 1841) * mm});
            skLineSegment(sketch, "E75.right", {"start": v(1132, 1813) * mm, "end": v(1132, 1841) * mm});
            skLineSegment(sketch, "E76.bottom", {"start": v(1148, 1813) * mm, "end": v(1176, 1813) * mm});
            skLineSegment(sketch, "E76.top", {"start": v(1148, 1841) * mm, "end": v(1176, 1841) * mm});
            skLineSegment(sketch, "E76.left", {"start": v(1148, 1813) * mm, "end": v(1148, 1841) * mm});
            skLineSegment(sketch, "E76.right", {"start": v(1176, 1813) * mm, "end": v(1176, 1841) * mm});
            skLineSegment(sketch, "E77.bottom", {"start": v(1666, 1813) * mm, "end": v(1694, 1813) * mm});
            skLineSegment(sketch, "E77.top", {"start": v(1666, 1841) * mm, "end": v(1694, 1841) * mm});
            skLineSegment(sketch, "E77.left", {"start": v(1666, 1813) * mm, "end": v(1666, 1841) * mm});
            skLineSegment(sketch, "E77.right", {"start": v(1694, 1813) * mm, "end": v(1694, 1841) * mm});
            skLineSegment(sketch, "E78.bottom", {"start": v(16, 1347) * mm, "end": v(44, 1347) * mm});
            skLineSegment(sketch, "E78.top", {"start": v(16, 1375) * mm, "end": v(44, 1375) * mm});
            skLineSegment(sketch, "E78.left", {"start": v(16, 1347) * mm, "end": v(16, 1375) * mm});
            skLineSegment(sketch, "E78.right", {"start": v(44, 1347) * mm, "end": v(44, 1375) * mm});
            skLineSegment(sketch, "E79.bottom", {"start": v(534, 1347) * mm, "end": v(562, 1347) * mm});
            skLineSegment(sketch, "E79.top", {"start": v(534, 1375) * mm, "end": v(562, 1375) * mm});
            skLineSegment(sketch, "E79.left", {"start": v(534, 1347) * mm, "end": v(534, 1375) * mm});
            skLineSegment(sketch, "E79.right", {"start": v(562, 1347) * mm, "end": v(562, 1375) * mm});
            skLineSegment(sketch, "E80.bottom", {"start": v(578, 972) * mm, "end": v(606, 972) * mm});
            skLineSegment(sketch, "E80.top", {"start": v(578, 1000) * mm, "end": v(606, 1000) * mm});
            skLineSegment(sketch, "E80.left", {"start": v(578, 972) * mm, "end": v(578, 1000) * mm});
            skLineSegment(sketch, "E80.right", {"start": v(606, 972) * mm, "end": v(606, 1000) * mm});
            skLineSegment(sketch, "E81.bottom", {"start": v(1104, 972) * mm, "end": v(1132, 972) * mm});
            skLineSegment(sketch, "E81.top", {"start": v(1104, 1000) * mm, "end": v(1132, 1000) * mm});
            skLineSegment(sketch, "E81.left", {"start": v(1104, 972) * mm, "end": v(1104, 1000) * mm});
            skLineSegment(sketch, "E81.right", {"start": v(1132, 972) * mm, "end": v(1132, 1000) * mm});
            skLineSegment(sketch, "E82.bottom", {"start": v(1148, 972) * mm, "end": v(1176, 972) * mm, "construction": true});
            skLineSegment(sketch, "E82.top", {"start": v(1148, 1000) * mm, "end": v(1176, 1000) * mm, "construction": true});
            skLineSegment(sketch, "E82.left", {"start": v(1148, 972) * mm, "end": v(1148, 1000) * mm, "construction": true});
            skLineSegment(sketch, "E82.right", {"start": v(1176, 972) * mm, "end": v(1176, 1000) * mm, "construction": true});
            skLineSegment(sketch, "E83.bottom", {"start": v(1666, 972) * mm, "end": v(1694, 972) * mm});
            skLineSegment(sketch, "E83.top", {"start": v(1666, 1000) * mm, "end": v(1694, 1000) * mm});
            skLineSegment(sketch, "E83.left", {"start": v(1666, 972) * mm, "end": v(1666, 1000) * mm});
            skLineSegment(sketch, "E83.right", {"start": v(1694, 972) * mm, "end": v(1694, 1000) * mm});
            skSolve(sketch);
        }
        {
            var Q0;
            Q0 = qSketchRegion(id + "F49", true);
            extrude(context, id + "F50", {"entities" : qUnion([Q0]), "depth" : 350 * mm, "offsetDistance" : 25 * mm});
        }
        {
            var Q0;
            Q0=makeQuery(id+"F14.opExtrude","CAP_FACE",FACE,{"disambiguationData":[OSD([sQuery(id+"F13.wireOp",EDGE,"E20.bottom"),sQuery(id+"F13.wireOp",EDGE,"E20.top"),sQuery(id+"F13.wireOp",EDGE,"E20.left"),sQuery(id+"F13.wireOp",EDGE,"E20.right")])],"isStart":false});
            var sketch = newSketch(context, id + "F51", { "sketchPlane" : qUnion([Q0])});
            skLineSegment(sketch, "E84.bottom", {"start": v(578, 0) * mm, "end": v(606, 0) * mm});
            skLineSegment(sketch, "E84.top", {"start": v(578, 28) * mm, "end": v(606, 28) * mm});
            skLineSegment(sketch, "E84.left", {"start": v(578, 0) * mm, "end": v(578, 28) * mm});
            skLineSegment(sketch, "E84.right", {"start": v(606, 0) * mm, "end": v(606, 28) * mm});
            skLineSegment(sketch, "E85.bottom", {"start": v(1148, 0) * mm, "end": v(1176, 0) * mm});
            skLineSegment(sketch, "E85.top", {"start": v(1148, 28) * mm, "end": v(1176, 28) * mm});
            skLineSegment(sketch, "E85.left", {"start": v(1148, 0) * mm, "end": v(1148, 28) * mm});
            skLineSegment(sketch, "E85.right", {"start": v(1176, 0) * mm, "end": v(1176, 28) * mm});
            skSolve(sketch);
        }
        {
            var Q0;
            Q0=makeQuery(id+"F51.imprint","IMPRINT",FACE,{"disambiguationData":[TD([[makeQuery(id+"F51.imprint","IMPRINT",EDGE,{"derivedFrom":sQuery(id+"F51.wireOp",EDGE,"E84.bottom")}),1.0]])]});
            var Q1;
            Q1=makeQuery(id+"F51.imprint","IMPRINT",FACE,{"disambiguationData":[TD([[makeQuery(id+"F51.imprint","IMPRINT",EDGE,{"derivedFrom":sQuery(id+"F51.wireOp",EDGE,"E85.bottom")}),1.0]])]});
            extrude(context, id + "F52", {"entities" : qUnion([Q0, Q1]), "depth" : 350 * mm, "offsetDistance" : 25 * mm});
        }
    });
